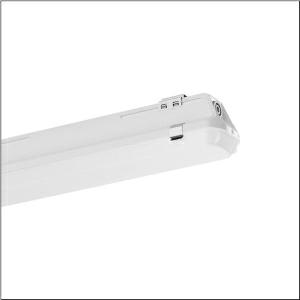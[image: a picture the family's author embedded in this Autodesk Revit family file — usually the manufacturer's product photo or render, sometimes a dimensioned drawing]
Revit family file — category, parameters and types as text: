
# Revit family: monsun_r__21_parking_51fg20dp440b_2f1b
name_source: partatom
category: Lighting Fixtures
units: mm (PartAtom-declared; Revit-internal decimal feet)

## family parameters
Cut with Voids When Loaded = No
Host = Face
Light Source = No
Part Type = Normal
Room Calculation Point = No
Round Connector Dimension = Use Diameter
Shared = No

## types (1)
- --- (1 x LED, 4810 lm, 34.4 W, 4000K)
    Apparent Load = 34 VA
    CIE Flux Codes = 45 75 93 94 100
    Color Rendering = 80
    Color Temperature = 4000K
    Default Elevation = 1800 mm
    Description = Monsun® 21 parking, damp-proof luminaire, chain hanger, primary optical cover: enclosure, of PC, light emission: direct distribution, primary light characteristic: symmetric, installation type: suspended mounting, surface-mounted, horizontal mounting, vertical mounting, LED, rated luminous flux: 4.810lm, luminous efficacy: 140lm/W, light colour: 840, colour temperature: 4000K, control gear: ECG DALI, with terminal, 5-pole, max. 2.5mm², mains connection: 220..240V, AC, 50/60Hz, rated input power: 34W, housing, of glass-fibre reinforced polyester, uncoated, bright grey, incl. chain hanger, length: 1.590mm, width: 90mm, height: 88mm, clip for enclosure, of stainless steel (V2A), ceiling mounting element, of stainless steel (V2A), chain hanger, of stainless steel (V2A), protection rating (complete): IP66, insulation class (complete): insulation class I (protective earthing), certification: CE, ENEC, VDE, UKCA, protection symbol: D, impact resistance: IK08, permissible operating ambient temperature: -25..+35°C, standard: EN 50419, EN 60598-2-1, corresponds to IFS (International Featured Standards) requirements for safety and quality in the food industry, for indoor or canopied outdoor use, no direct snow, no direct sun, no direct rain, contact your sales advisor before using the luminaires in applications with unclear chemical exposure, large temperature fluctuations or condensation-forming humidity, LABS conformity tested according to VDMA 24364:2018-05, packaging unit: 1 piece
    Height = 89 mm
    Lamp = 1 x LED
    Lamp Light Flux = 4810 lm
    Lamp Power = 34.4 W
    Lamp count = 1
    Length = 1590 mm
    Luminous efficacy = 140 lm/W
    Manufacturer = Siteco
    ModVariant = No
    Model = 51FG20DP440B
    Mounting Place = Ceiling
    Mounting Type = Surface mounted
    Number of Poles = 1
    OnlyDefault = Yes
    Power Factor = 1
    Product Name = Monsun® 21 parking
    Product group = damp-proof luminaire
    ProductGroupID = 301
    Protection Class = Protection class I
    Protection Degree = IP 66
    RLX_Detail_Level = 1
    RLX_Emergency_Light_Flux = 0 lm
    RLX_Emergency_Type = 0
    RLX_Emergency_Type_DB = No
    RlxData = <blob elided: 92329 chars, md5=17d71f24>
    Socket = socket
    Standby Power = 0 W
    System Light Flux = 4810 lm
    System Power = 34 W
    Type Comments = factory setting: luminous flux: 100 % | dim-lin: 254 | 228 mA
    Type Image = l_1006717.jpg
    URL = http://relux.com
    VarID = @adj_152095
    Voltage = 0 V
    Weight = 0.00 kg
    Width = 90 mm

## geometry (parser evidence)
native form markers: Blend x4, Sweep x13
no freeform markers — native parametric forms only
